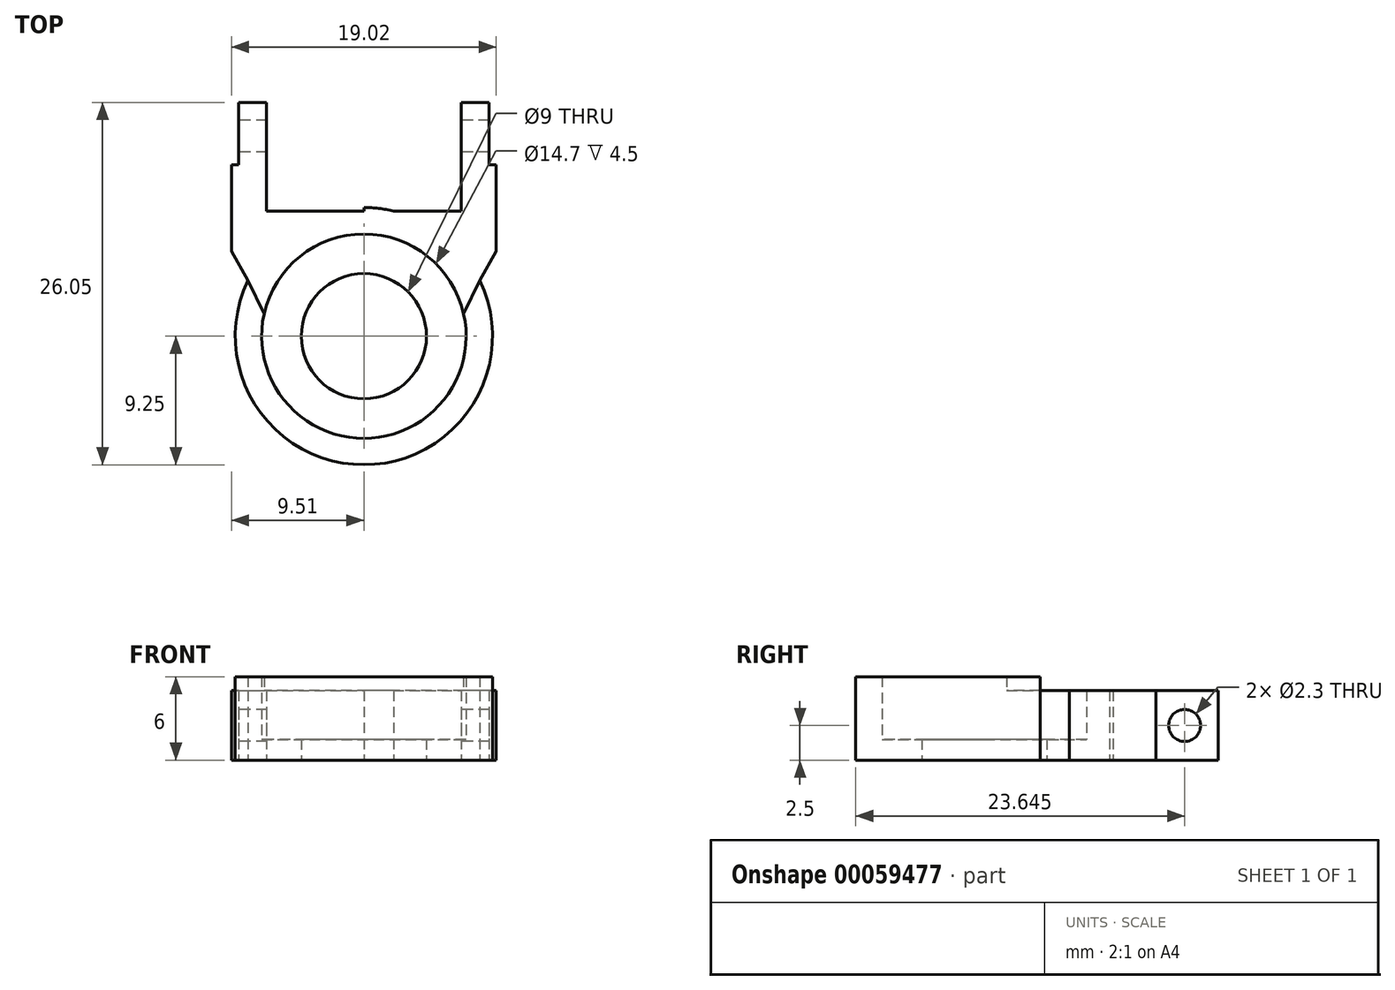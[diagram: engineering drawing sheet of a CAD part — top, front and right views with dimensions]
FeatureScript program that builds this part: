
annotation { "Feature Type Name" : "Feature", "Feature Type Description" : "" }
export const myFeature = defineFeature(function(context is Context, id is Id, definition is map)
    precondition{}
    {
        {
            var Q0;
            Q0=qCreatedBy(makeId("Top.planeOp"),FACE);
            var sketch = newSketch(context, id + "F0", { "sketchPlane" : qUnion([Q0])});
            skLineSegment(sketch, "E0", {"start": v(-65.2, 0) * mm, "end": v(71.29, 0) * mm, "construction": true});
            skLineSegment(sketch, "E1", {"start": v(0, 54.68) * mm, "end": v(0, -53.77) * mm, "construction": true});
            skLineSegment(sketch, "E2.0", {"start": v(7, 54.68) * mm, "end": v(7, -53.77) * mm, "construction": true});
            skLineSegment(sketch, "E3.0", {"start": v(-7, 54.68) * mm, "end": v(-7, -53.77) * mm, "construction": true});
            skCircle(sketch, "E4", {"center": v(0, 0) * mm, "radius": 4.5 * mm});
            skCircle(sketch, "E5", {"center": v(0, 0) * mm, "radius": 7.35 * mm});
            skCircle(sketch, "E6", {"center": v(0, 0) * mm, "radius": 9.25 * mm});
            skLineSegment(sketch, "E7.0", {"start": v(-65.2, 9) * mm, "end": v(71.29, 9) * mm});
            skLineSegment(sketch, "E8", {"start": v(-7, 9) * mm, "end": v(-7, 12.34) * mm});
            skLineSegment(sketch, "E9", {"start": v(-7, 12.34) * mm, "end": v(-9.51, 12.34) * mm});
            skLineSegment(sketch, "E10", {"start": v(-9.51, 12.34) * mm, "end": v(-9.51, 6.1) * mm});
            skLineSegment(sketch, "E11", {"start": v(-9.51, 6.1) * mm, "end": v(-8.33, 4.01) * mm});
            skLineSegment(sketch, "E12", {"start": v(0, 9.25) * mm, "end": v(0, 9) * mm});
            skLineSegment(sketch, "E13.MirrorCS", {"start": v(65.2, 9) * mm, "end": v(-71.29, 9) * mm});
            skLineSegment(sketch, "E14.MirrorCS", {"start": v(7, 9) * mm, "end": v(7, 12.34) * mm});
            skLineSegment(sketch, "E15.MirrorCS", {"start": v(7, 12.34) * mm, "end": v(9.51, 12.34) * mm});
            skLineSegment(sketch, "E16.MirrorCS", {"start": v(9.51, 12.34) * mm, "end": v(9.51, 6.1) * mm});
            skLineSegment(sketch, "E17.MirrorCS", {"start": v(9.51, 6.1) * mm, "end": v(8.33, 4.01) * mm});
            skLineSegment(sketch, "E18", {"start": v(-8.33, 4.01) * mm, "end": v(-7.17, 1.6) * mm});
            skLineSegment(sketch, "E19.MirrorCS", {"start": v(8.33, 4.01) * mm, "end": v(7.17, 1.6) * mm});
            skLineSegment(sketch, "E20", {"start": v(-7, 12.34) * mm, "end": v(-7, 16.8) * mm});
            skLineSegment(sketch, "E21.0", {"start": v(-9, 12.34) * mm, "end": v(-9, 16.8) * mm});
            skLineSegment(sketch, "E22", {"start": v(-9, 16.8) * mm, "end": v(-7, 16.8) * mm});
            skLineSegment(sketch, "E23.MirrorCS", {"start": v(9, 16.8) * mm, "end": v(7, 16.8) * mm});
            skLineSegment(sketch, "E24.MirrorCS", {"start": v(9, 12.34) * mm, "end": v(9, 16.8) * mm});
            skLineSegment(sketch, "E25.MirrorCS", {"start": v(-14, 54.68) * mm, "end": v(-14, -53.77) * mm, "construction": true});
            skLineSegment(sketch, "E26.MirrorCS", {"start": v(7, 12.34) * mm, "end": v(7, 16.8) * mm});
            skSolve(sketch);
        }
        {
            var Q0;
            Q0=makeQuery(id+"F0.imprint","IMPRINT",FACE,{"disambiguationData":[TD([[makeQuery(id+"F0.imprint","IMPRINT",EDGE,{"derivedFrom":sQuery(id+"F0.wireOp",EDGE,"E4")}),-1.0]])]});
            extrude(context, id + "F1", {"entities" : qUnion([Q0]), "depth" : 1.5 * mm});
        }
        {
            var Q0;
            {var subQ0=sQuery(id+"F0.wireOp",EDGE,"E8");Q0=makeQuery(id+"F0.imprint","IMPRINT",FACE,{"disambiguationData":[TD([[makeQuery(id+"F0.imprint","IMPRINT",EDGE,{"derivedFrom":subQ0}),1.0]])]});}
            var Q1;
            {var subQ1=sQuery(id+"F0.wireOp",EDGE,"E11");Q1=makeQuery(id+"F0.imprint","IMPRINT",FACE,{"disambiguationData":[TD([[makeQuery(id+"F0.imprint","IMPRINT",EDGE,{"derivedFrom":subQ1}),1.0]])]});}
            var Q2;
            {var subQ0=sQuery(id+"F0.wireOp",EDGE,"E18");Q2=makeQuery(id+"F0.imprint","IMPRINT",FACE,{"disambiguationData":[TD([[makeQuery(id+"F0.imprint","IMPRINT",EDGE,{"derivedFrom":subQ0}),1.0]])]});}
            var Q3;
            {var subQ1=sQuery(id+"F0.wireOp",EDGE,"E12");Q3=makeQuery(id+"F0.imprint","IMPRINT",FACE,{"disambiguationData":[TD([[makeQuery(id+"F0.imprint","IMPRINT",EDGE,{"derivedFrom":subQ1}),1.0]])]});}
            var Q4;
            {var subQ0=sQuery(id+"F0.wireOp",EDGE,"E14.MirrorCS");Q4=makeQuery(id+"F0.imprint","IMPRINT",FACE,{"disambiguationData":[TD([[makeQuery(id+"F0.imprint","IMPRINT",EDGE,{"derivedFrom":subQ0}),-1.0]])]});}
            var Q5;
            {var subQ0=sQuery(id+"F0.wireOp",EDGE,"E20");Q5=makeQuery(id+"F0.imprint","IMPRINT",FACE,{"disambiguationData":[TD([[makeQuery(id+"F0.imprint","IMPRINT",EDGE,{"derivedFrom":subQ0}),1.0]])]});}
            var Q6;
            Q6=makeQuery(id+"F0.imprint","IMPRINT",FACE,{"disambiguationData":[TD([[makeQuery(id+"F0.imprint","IMPRINT",EDGE,{"derivedFrom":sQuery(id+"F0.wireOp",EDGE,"E23.MirrorCS")}),1.0]])]});
            var Q7;
            {var subQ0=sQuery(id+"F0.wireOp",EDGE,"E17.MirrorCS");Q7=makeQuery(id+"F0.imprint","IMPRINT",FACE,{"disambiguationData":[TD([[makeQuery(id+"F0.imprint","IMPRINT",EDGE,{"derivedFrom":subQ0}),-1.0]])]});}
            extrude(context, id + "F2", {"entities" : qUnion([Q0, Q1, Q2, Q3, Q4, Q5, Q6, Q7]), "operationType" : NewBodyOperationType.ADD, "depth" : 5 * mm});
        }
        {
            var Q0;
            {var subQ0=sQuery(id+"F0.wireOp",EDGE,"E18");Q0=makeQuery(id+"F0.imprint","IMPRINT",FACE,{"disambiguationData":[TD([[makeQuery(id+"F0.imprint","IMPRINT",EDGE,{"derivedFrom":subQ0}),-1.0]])]});}
            extrude(context, id + "F3", {"entities" : qUnion([Q0]), "operationType" : NewBodyOperationType.ADD, "depth" : 6 * mm});
        }
        {
            var Q0;
            Q0=makeQuery(id+"F2.opExtrude","SWEPT_FACE",FACE,{"disambiguationData":[OSD([sQuery(id+"F0.wireOp",EDGE,"E21.0")])]});
            var sketch = newSketch(context, id + "F4", { "sketchPlane" : qUnion([Q0])});
            skLineSegment(sketch, "E27.0", {"start": v(-12.34, 5) * mm, "end": v(-16.8, 5) * mm});
            skLineSegment(sketch, "E28.0", {"start": v(-12.34, 0) * mm, "end": v(-16.8, 0) * mm});
            skLineSegment(sketch, "E29.0", {"start": v(-16.8, 5) * mm, "end": v(-16.8, 0) * mm});
            skLineSegment(sketch, "E30", {"start": v(-14.57, 5) * mm, "end": v(-14.22, 0) * mm, "construction": true});
            skCircle(sketch, "E31", {"center": v(-14.4, 2.5) * mm, "radius": 1.15 * mm});
            skSolve(sketch);
        }
        {
            var Q0;
            Q0=makeQuery(id+"F4.imprint","IMPRINT",FACE,{"disambiguationData":[TD([[makeQuery(id+"F4.imprint","IMPRINT",EDGE,{"derivedFrom":sQuery(id+"F4.wireOp",EDGE,"E31")}),1.0]])]});
            var Q1;
            Q1=sQuery(id+"F4.wireOp",EDGE,"E31");
            extrude(context, id + "F5", {"entities" : qUnion([Q0]), "operationType" : NewBodyOperationType.REMOVE, "surfaceEntities" : qUnion([Q1]), "oppositeDirection" : true, "depth" : 25 * mm});
        }
    });
